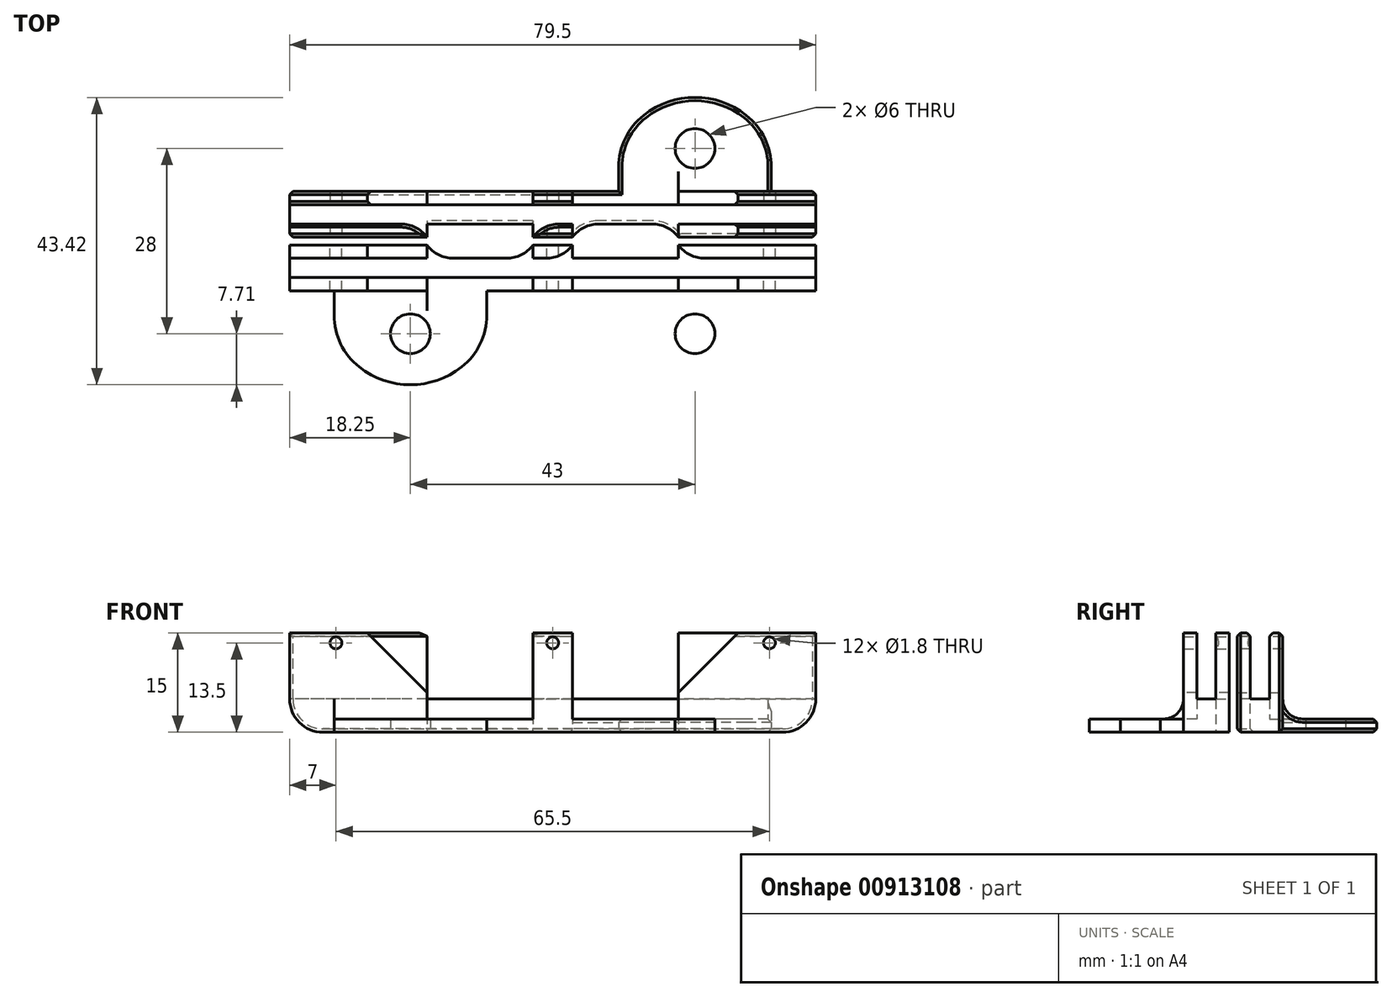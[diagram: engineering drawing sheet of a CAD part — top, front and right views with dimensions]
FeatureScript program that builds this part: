
annotation { "Feature Type Name" : "Feature", "Feature Type Description" : "" }
export const myFeature = defineFeature(function(context is Context, id is Id, definition is map)
    precondition{}
    {
        {
            var Q0;
            Q0=qCreatedBy(makeId("Top.planeOp"),FACE);
            var sketch = newSketch(context, id + "F0", { "sketchPlane" : qUnion([Q0])});
            skLineSegment(sketch, "E0", {"start": v(-39.75, 6.5) * mm, "end": v(39.75, 6.5) * mm});
            skPoint(sketch, "E1", {"position": v(-21.5, 0) * mm});
            skPoint(sketch, "E2", {"position": v(21.5, 0) * mm});
            skLineSegment(sketch, "E3", {"start": v(-21.5, 0) * mm, "end": v(21.5, 0) * mm, "construction": true});
            skLineSegment(sketch, "E4", {"start": v(0, 0) * mm, "end": v(0, 34.78) * mm, "construction": true});
            skPoint(sketch, "E5", {"position": v(0, 6.5) * mm});
            skCircle(sketch, "E6", {"center": v(-21.5, 0) * mm, "radius": 3 * mm});
            skCircle(sketch, "E7.MirrorC", {"center": v(21.5, 0) * mm, "radius": 3 * mm});
            skLineSegment(sketch, "E8", {"start": v(-21.5, 0) * mm, "end": v(-21.5, 46.29) * mm, "construction": true});
            skPoint(sketch, "E9.center.orphan", {"position": v(-21.5, -3) * mm});
            skPoint(sketch, "E10", {"position": v(-21.5, 3) * mm});
            skLineSegment(sketch, "E11", {"start": v(-39.75, 8.5) * mm, "end": v(39.75, 8.5) * mm});
            skLineSegment(sketch, "E12", {"start": v(-39.75, 6.5) * mm, "end": v(-39.75, 13.4) * mm});
            skLineSegment(sketch, "E13.MirrorCS", {"start": v(39.75, 6.5) * mm, "end": v(39.75, 13.4) * mm});
            skLineSegment(sketch, "E14", {"start": v(-39.75, 13.4) * mm, "end": v(39.75, 13.4) * mm});
            skLineSegment(sketch, "E15", {"start": v(-39.75, 11.4) * mm, "end": v(39.75, 11.4) * mm});
            skLineSegment(sketch, "E16", {"start": v(-19, 13.4) * mm, "end": v(-19, 6.5) * mm});
            skLineSegment(sketch, "E17.MirrorCS", {"start": v(19, 13.4) * mm, "end": v(19, 6.5) * mm});
            skLineSegment(sketch, "E18", {"start": v(-3, 6.5) * mm, "end": v(-3, 13.4) * mm});
            skLineSegment(sketch, "E19.MirrorCS", {"start": v(3, 6.5) * mm, "end": v(3, 13.4) * mm});
            skArc(sketch, "E20", {"start": v(-29.24, -5.03) * mm, "mid": v(-21.5, -7.71) * mm, "end": v(-13.76, -5.03) * mm});
            skLineSegment(sketch, "E21", {"start": v(-33.05, 2.82) * mm, "end": v(-33.05, 6.5) * mm});
            skLineSegment(sketch, "E22.MirrorCS", {"start": v(-9.95, 2.82) * mm, "end": v(-9.95, 6.5) * mm});
            skLineSegment(sketch, "E23.MirrorCS", {"start": v(9.95, 2.82) * mm, "end": v(9.95, 6.5) * mm});
            skLineSegment(sketch, "E24.MirrorCS", {"start": v(33.05, 2.82) * mm, "end": v(33.05, 6.5) * mm});
            skArc(sketch, "E25.MirrorCS", {"start": v(29.24, -5.03) * mm, "mid": v(21.5, -7.71) * mm, "end": v(13.76, -5.03) * mm});
            skPoint(sketch, "E26.visualSharp", {"position": v(-33.05, 0) * mm});
            skArc(sketch, "E26.filletArc", {"start": v(-33.05, 2.82) * mm, "mid": v(-32.04, -1.54) * mm, "end": v(-29.24, -5.03) * mm});
            skPoint(sketch, "E27.visualSharp", {"position": v(-9.95, 0) * mm});
            skArc(sketch, "E27.filletArc", {"start": v(-13.76, -5.03) * mm, "mid": v(-10.96, -1.54) * mm, "end": v(-9.95, 2.82) * mm});
            skPoint(sketch, "E28.visualSharp", {"position": v(9.95, 0) * mm});
            skArc(sketch, "E28.filletArc", {"start": v(9.95, 2.82) * mm, "mid": v(10.96, -1.54) * mm, "end": v(13.76, -5.03) * mm});
            skPoint(sketch, "E29.visualSharp", {"position": v(33.05, 0) * mm});
            skArc(sketch, "E29.filletArc", {"start": v(29.24, -5.03) * mm, "mid": v(32.04, -1.54) * mm, "end": v(33.05, 2.82) * mm});
            skSolve(sketch);
        }
        {
            var Q0;
            {var subQ0=sQuery(id+"F0.wireOp",EDGE,"E11");Q0=makeQuery(id+"F0.imprint","IMPRINT",FACE,{"disambiguationData":[TD([[makeQuery(id+"F0.imprint","IMPRINT",EDGE,{"derivedFrom":subQ0}),1.0]])]});}
            extrude(context, id + "F1", {"entities" : qUnion([Q0]), "depth" : 5 * mm, "offsetDistance" : 25 * mm});
        }
        {
            var Q0;
            Q0=makeQuery(id+"F0.imprint","IMPRINT",FACE,{"disambiguationData":[TD([[makeQuery(id+"F0.imprint","IMPRINT",EDGE,{"derivedFrom":sQuery(id+"F0.wireOp",EDGE,"E6")}),-1.0]])]});
            var Q1;
            Q1=makeQuery(id+"F0.imprint","IMPRINT",FACE,{"disambiguationData":[TD([[makeQuery(id+"F0.imprint","IMPRINT",EDGE,{"derivedFrom":sQuery(id+"F0.wireOp",EDGE,"E7.MirrorC")}),1.0]])]});
            var Q2;
            {var subQ1=sQuery(id+"F0.wireOp",EDGE,"E0");var subQ5=sQuery(id+"F0.wireOp",EDGE,"E19.MirrorCS");var subQ8=makeQuery(id+"F0.imprint","INTERSECT",VERTEX,{"derivedFrom":[subQ1,subQ5]});Q2=makeQuery(id+"F0.imprint","IMPRINT",FACE,{"disambiguationData":[TD([[makeQuery(id+"F0.imprint","IMPRINT",EDGE,{"disambiguationData":[TD([[subQ8,-1.0]])],"derivedFrom":subQ1}),1.0]])]});}
            var Q3;
            {var subQ1=sQuery(id+"F0.wireOp",EDGE,"E0");var subQ6=sQuery(id+"F0.wireOp",EDGE,"E17.MirrorCS");var subQ8=makeQuery(id+"F0.imprint","INTERSECT",VERTEX,{"derivedFrom":[subQ1,subQ6]});Q3=makeQuery(id+"F0.imprint","IMPRINT",FACE,{"disambiguationData":[TD([[makeQuery(id+"F0.imprint","IMPRINT",EDGE,{"disambiguationData":[TD([[subQ8,-1.0]])],"derivedFrom":subQ1}),1.0]])]});}
            var Q4;
            {var subQ0=sQuery(id+"F0.wireOp",EDGE,"E18");var subQ1=sQuery(id+"F0.wireOp",EDGE,"E0");var subQ2=makeQuery(id+"F0.imprint","INTERSECT",VERTEX,{"derivedFrom":[subQ1,subQ0]});Q4=makeQuery(id+"F0.imprint","IMPRINT",FACE,{"disambiguationData":[TD([[makeQuery(id+"F0.imprint","IMPRINT",EDGE,{"disambiguationData":[TD([[subQ2,-1.0]])],"derivedFrom":subQ1}),1.0]])]});}
            var Q5;
            {var subQ0=sQuery(id+"F0.wireOp",EDGE,"E16");var subQ1=sQuery(id+"F0.wireOp",EDGE,"E0");var subQ2=makeQuery(id+"F0.imprint","INTERSECT",VERTEX,{"derivedFrom":[subQ1,subQ0]});Q5=makeQuery(id+"F0.imprint","IMPRINT",FACE,{"disambiguationData":[TD([[makeQuery(id+"F0.imprint","IMPRINT",EDGE,{"disambiguationData":[TD([[subQ2,-1.0]])],"derivedFrom":subQ1}),1.0]])]});}
            extrude(context, id + "F2", {"entities" : qUnion([Q0, Q1, Q2, Q3, Q4, Q5]), "operationType" : NewBodyOperationType.ADD, "depth" : 2 * mm, "offsetDistance" : 25 * mm});
        }
        {
            var Q0;
            {var subQ0=sQuery(id+"F0.wireOp",EDGE,"E12");var subQ1=sQuery(id+"F0.wireOp",EDGE,"E0");var subQ2=makeQuery(id+"F0.imprint","INTERSECT",VERTEX,{"derivedFrom":[subQ1,subQ0]});Q0=makeQuery(id+"F0.imprint","IMPRINT",FACE,{"disambiguationData":[TD([[makeQuery(id+"F0.imprint","IMPRINT",EDGE,{"disambiguationData":[TD([[subQ2,-1.0]])],"derivedFrom":subQ1}),1.0]])]});}
            var Q1;
            {var subQ1=sQuery(id+"F0.wireOp",EDGE,"E0");var subQ6=sQuery(id+"F0.wireOp",EDGE,"E17.MirrorCS");var subQ8=makeQuery(id+"F0.imprint","INTERSECT",VERTEX,{"derivedFrom":[subQ1,subQ6]});Q1=makeQuery(id+"F0.imprint","IMPRINT",FACE,{"disambiguationData":[TD([[makeQuery(id+"F0.imprint","IMPRINT",EDGE,{"disambiguationData":[TD([[subQ8,-1.0]])],"derivedFrom":subQ1}),1.0]])]});}
            var Q2;
            {var subQ0=sQuery(id+"F0.wireOp",EDGE,"E14");var subQ1=sQuery(id+"F0.wireOp",EDGE,"E12");var subQ2=makeQuery(id+"F0.imprint","INTERSECT",VERTEX,{"derivedFrom":[subQ1,subQ0]});Q2=makeQuery(id+"F0.imprint","IMPRINT",FACE,{"disambiguationData":[TD([[makeQuery(id+"F0.imprint","IMPRINT",EDGE,{"disambiguationData":[TD([[subQ2,1.0]])],"derivedFrom":subQ1}),-1.0]])]});}
            var Q3;
            {var subQ0=sQuery(id+"F0.wireOp",EDGE,"E14");var subQ1=sQuery(id+"F0.wireOp",EDGE,"E13.MirrorCS");var subQ2=makeQuery(id+"F0.imprint","INTERSECT",VERTEX,{"derivedFrom":[subQ1,subQ0]});Q3=makeQuery(id+"F0.imprint","IMPRINT",FACE,{"disambiguationData":[TD([[makeQuery(id+"F0.imprint","IMPRINT",EDGE,{"disambiguationData":[TD([[subQ2,1.0]])],"derivedFrom":subQ1}),1.0]])]});}
            var Q4;
            {var subQ0=sQuery(id+"F0.wireOp",EDGE,"E18");var subQ1=sQuery(id+"F0.wireOp",EDGE,"E14");var subQ2=makeQuery(id+"F0.imprint","INTERSECT",VERTEX,{"derivedFrom":[subQ1,subQ0]});Q4=makeQuery(id+"F0.imprint","IMPRINT",FACE,{"disambiguationData":[TD([[makeQuery(id+"F0.imprint","IMPRINT",EDGE,{"disambiguationData":[TD([[subQ2,-1.0]])],"derivedFrom":subQ1}),-1.0]])]});}
            var Q5;
            {var subQ0=sQuery(id+"F0.wireOp",EDGE,"E18");var subQ1=sQuery(id+"F0.wireOp",EDGE,"E0");var subQ2=makeQuery(id+"F0.imprint","INTERSECT",VERTEX,{"derivedFrom":[subQ1,subQ0]});Q5=makeQuery(id+"F0.imprint","IMPRINT",FACE,{"disambiguationData":[TD([[makeQuery(id+"F0.imprint","IMPRINT",EDGE,{"disambiguationData":[TD([[subQ2,-1.0]])],"derivedFrom":subQ1}),1.0]])]});}
            extrude(context, id + "F3", {"entities" : qUnion([Q0, Q1, Q2, Q3, Q4, Q5]), "operationType" : NewBodyOperationType.ADD, "depth" : 15 * mm, "offsetDistance" : 25 * mm});
        }
        {
            var Q0;
            {var subQ0=sQuery(id+"F0.wireOp",EDGE,"E0");Q0=makeQuery(id+"F3.boolean.opBoolean","INTERSECT",EDGE,{"derivedFrom":[makeQuery(id+"F2.opExtrude","CAP_FACE",FACE,{"disambiguationData":[OSD([subQ0,sQuery(id+"F0.wireOp",EDGE,"E6"),sQuery(id+"F0.wireOp",EDGE,"E11"),sQuery(id+"F0.wireOp",EDGE,"E12"),sQuery(id+"F0.wireOp",EDGE,"E13.MirrorCS"),sQuery(id+"F0.wireOp",EDGE,"E20"),sQuery(id+"F0.wireOp",EDGE,"E21"),sQuery(id+"F0.wireOp",EDGE,"E22.MirrorCS"),sQuery(id+"F0.wireOp",EDGE,"E26.filletArc"),sQuery(id+"F0.wireOp",EDGE,"E27.filletArc")])],"isStart":false}),makeQuery(id+"F3.opExtrude","SWEPT_FACE",FACE,{"disambiguationData":[OSD([subQ0])]})]});}
            var Q1;
            {var subQ0=sQuery(id+"F0.wireOp",EDGE,"E0");Q1=makeQuery(id+"F2.opExtrude","CAP_EDGE",EDGE,{"disambiguationData":[OSD([subQ0]),TDD([makeQuery(id+"F0.imprint","IMPRINT",EDGE,{"disambiguationData":[TD([[makeQuery(id+"F0.imprint","INTERSECT",VERTEX,{"derivedFrom":[subQ0,sQuery(id+"F0.wireOp",EDGE,"E16")]}),1.0]])],"derivedFrom":subQ0})])],"isStart":false});}
            fillet(context, id + "F4", {"entities" : qUnion([Q0, Q1]), "radius" : 3 * mm, "tangentPropagation" : true, "allowEdgeOverflow" : false});
        }
        {
            var Q0;
            {var subQ0=sQuery(id+"F0.wireOp",EDGE,"E15");var subQ1=sQuery(id+"F0.wireOp",EDGE,"E17.MirrorCS");Q0=makeQuery(id+"F3.boolean.opBoolean","SPLIT",EDGE,{"disambiguationData":[topologyDisambiguationEdgeConnected([makeQuery(id+"F1.opExtrude","SWEPT_FACE",FACE,{"disambiguationData":[OSD([subQ0])]})])],"derivedFrom":makeQuery(id+"F3.opExtrude","SWEPT_EDGE",EDGE,{"disambiguationData":[OSD([subQ0,subQ1])]})});}
            var Q1;
            {var subQ0=sQuery(id+"F0.wireOp",EDGE,"E15");var subQ1=sQuery(id+"F0.wireOp",EDGE,"E19.MirrorCS");Q1=makeQuery(id+"F3.boolean.opBoolean","SPLIT",EDGE,{"disambiguationData":[topologyDisambiguationEdgeConnected([makeQuery(id+"F1.opExtrude","SWEPT_FACE",FACE,{"disambiguationData":[OSD([subQ0])]})])],"derivedFrom":makeQuery(id+"F3.opExtrude","SWEPT_EDGE",EDGE,{"disambiguationData":[OSD([subQ0,subQ1])]})});}
            var Q2;
            {var subQ0=sQuery(id+"F0.wireOp",EDGE,"E15");var subQ1=sQuery(id+"F0.wireOp",EDGE,"E18");Q2=makeQuery(id+"F3.boolean.opBoolean","SPLIT",EDGE,{"disambiguationData":[topologyDisambiguationEdgeConnected([makeQuery(id+"F1.opExtrude","SWEPT_FACE",FACE,{"disambiguationData":[OSD([subQ0])]})])],"derivedFrom":makeQuery(id+"F3.opExtrude","SWEPT_EDGE",EDGE,{"disambiguationData":[OSD([subQ0,subQ1])]})});}
            var Q3;
            {var subQ0=sQuery(id+"F0.wireOp",EDGE,"E15");var subQ1=sQuery(id+"F0.wireOp",EDGE,"E16");Q3=makeQuery(id+"F3.boolean.opBoolean","SPLIT",EDGE,{"disambiguationData":[topologyDisambiguationEdgeConnected([makeQuery(id+"F1.opExtrude","SWEPT_FACE",FACE,{"disambiguationData":[OSD([subQ0])]})])],"derivedFrom":makeQuery(id+"F3.opExtrude","SWEPT_EDGE",EDGE,{"disambiguationData":[OSD([subQ0,subQ1])]})});}
            fillet(context, id + "F5", {"entities" : qUnion([Q0, Q1, Q2, Q3]), "radius" : 5 * mm, "tangentPropagation" : true, "allowEdgeOverflow" : false});
        }
        {
            var Q0;
            {var subQ0=sQuery(id+"F0.wireOp",EDGE,"E14");Q0=makeQuery(id+"F3.opExtrude","SWEPT_FACE",FACE,{"disambiguationData":[OSD([subQ0]),TDD([makeQuery(id+"F0.imprint","IMPRINT",EDGE,{"disambiguationData":[TD([[makeQuery(id+"F0.imprint","INTERSECT",VERTEX,{"derivedFrom":[sQuery(id+"F0.wireOp",EDGE,"E13.MirrorCS"),subQ0]}),1.0]])],"derivedFrom":subQ0})])]});}
            var sketch = newSketch(context, id + "F6", { "sketchPlane" : qUnion([Q0])});
            skPoint(sketch, "E30", {"position": v(-32.75, 13.5) * mm});
            skPoint(sketch, "E31", {"position": v(0, 13.5) * mm});
            skPoint(sketch, "E32.MirrorP", {"position": v(32.75, 13.5) * mm});
            skSolve(sketch);
        }
        {
            var Q0;
            Q0=sQuery(id+"F6.wireOp",VERTEX,"E30");
            var Q1;
            Q1=sQuery(id+"F6.wireOp",VERTEX,"E31");
            var Q2;
            Q2=sQuery(id+"F6.wireOp",VERTEX,"E32.MirrorP");
            var Q3;
            Q3=makeQuery(id+"F1.opExtrude","SWEPT_BODY",BODY,{"disambiguationData":[OSD([sQuery(id+"F0.wireOp",EDGE,"E11"),sQuery(id+"F0.wireOp",EDGE,"E12"),sQuery(id+"F0.wireOp",EDGE,"E13.MirrorCS"),sQuery(id+"F0.wireOp",EDGE,"E15")])]});
            hole(context, id + "F7", {"style" : HoleStyle.SIMPLE, "endStyle" : HoleEndStyle.THROUGH, "holeDiameter" : 1.8 * mm, "majorDiameter" : 5 * mm, "isTappedThrough" : true, "tappedDepth" : 12 * mm, "tapClearance" : 3, "locations" : qUnion([Q0, Q1, Q2]), "scope" : qUnion([Q3])});
        }
        {
            var Q0;
            {var subQ0=sQuery(id+"F0.wireOp",EDGE,"E16");Q0=makeQuery(id+"F3.opExtrude","CAP_EDGE",EDGE,{"disambiguationData":[OSD([subQ0]),TDD([makeQuery(id+"F0.imprint","IMPRINT",EDGE,{"disambiguationData":[TD([[makeQuery(id+"F0.imprint","INTERSECT",VERTEX,{"derivedFrom":[sQuery(id+"F0.wireOp",EDGE,"E0"),subQ0]}),1.0]])],"derivedFrom":subQ0})])],"isStart":false});}
            var Q1;
            {var subQ0=sQuery(id+"F0.wireOp",EDGE,"E16");Q1=makeQuery(id+"F3.opExtrude","CAP_EDGE",EDGE,{"disambiguationData":[OSD([subQ0]),TDD([makeQuery(id+"F0.imprint","IMPRINT",EDGE,{"disambiguationData":[TD([[makeQuery(id+"F0.imprint","INTERSECT",VERTEX,{"derivedFrom":[sQuery(id+"F0.wireOp",EDGE,"E14"),subQ0]}),-1.0]])],"derivedFrom":subQ0})])],"isStart":false});}
            var Q2;
            {var subQ0=sQuery(id+"F0.wireOp",EDGE,"E17.MirrorCS");Q2=makeQuery(id+"F3.opExtrude","CAP_EDGE",EDGE,{"disambiguationData":[OSD([subQ0]),TDD([makeQuery(id+"F0.imprint","IMPRINT",EDGE,{"disambiguationData":[TD([[makeQuery(id+"F0.imprint","INTERSECT",VERTEX,{"derivedFrom":[sQuery(id+"F0.wireOp",EDGE,"E0"),subQ0]}),1.0]])],"derivedFrom":subQ0})])],"isStart":false});}
            var Q3;
            {var subQ0=sQuery(id+"F0.wireOp",EDGE,"E17.MirrorCS");Q3=makeQuery(id+"F3.opExtrude","CAP_EDGE",EDGE,{"disambiguationData":[OSD([subQ0]),TDD([makeQuery(id+"F0.imprint","IMPRINT",EDGE,{"disambiguationData":[TD([[makeQuery(id+"F0.imprint","INTERSECT",VERTEX,{"derivedFrom":[sQuery(id+"F0.wireOp",EDGE,"E14"),subQ0]}),-1.0]])],"derivedFrom":subQ0})])],"isStart":false});}
            chamfer(context, id + "F8", {"entities" : qUnion([Q0, Q1, Q2, Q3]), "width" : 9 * mm, "tangentPropagation" : true});
        }
        {
            var Q0;
            Q0=makeQuery(id+"F1.opExtrude","SWEPT_BODY",BODY,{"disambiguationData":[OSD([sQuery(id+"F0.wireOp",EDGE,"E11"),sQuery(id+"F0.wireOp",EDGE,"E12"),sQuery(id+"F0.wireOp",EDGE,"E13.MirrorCS"),sQuery(id+"F0.wireOp",EDGE,"E15")])]});
            transform(context, id + "F9", {"entities" : qUnion([Q0]), "transformType" : TransformType.TRANSLATION_3D, "dx" : 6 * mm, "dy" : 15 * mm, "dz" : 0 * mm, "makeCopy" : true});
        }
        {
            var Q0;
            Q0=makeQuery(id+"F9.opPattern","COPY",BODY,{"derivedFrom":makeQuery(id+"F1.opExtrude","SWEPT_BODY",BODY,{"disambiguationData":[OSD([sQuery(id+"F0.wireOp",EDGE,"E11"),sQuery(id+"F0.wireOp",EDGE,"E12"),sQuery(id+"F0.wireOp",EDGE,"E13.MirrorCS"),sQuery(id+"F0.wireOp",EDGE,"E15")])]}),"instanceName":"1"});
            var Q1;
            Q1=makeQuery(id+"F9.opPattern","COPY",EDGE,{"derivedFrom":makeQuery(id+"F3.opExtrude","SWEPT_EDGE",EDGE,{"disambiguationData":[OSD([sQuery(id+"F0.wireOp",EDGE,"E0"),sQuery(id+"F0.wireOp",EDGE,"E18")])]}),"instanceName":"1"});
            transform(context, id + "F10", {"entities" : qUnion([Q0]), "transformType" : TransformType.ROTATION, "transformAxis" : qUnion([Q1]), "angle" : 180 * degree, "makeCopy" : false});
        }
        {
            var Q0;
            {var subQ0=sQuery(id+"F0.wireOp",EDGE,"E12");Q0=makeQuery(id+"F3.boolean.opBoolean","MERGE",EDGE,{"derivedFrom":[makeQuery(id+"F1.opExtrude","CAP_EDGE",EDGE,{"disambiguationData":[OSD([subQ0])],"isStart":true}),makeQuery(id+"F3.opExtrude","CAP_EDGE",EDGE,{"disambiguationData":[OSD([subQ0]),TDD([makeQuery(id+"F0.imprint","IMPRINT",EDGE,{"disambiguationData":[TD([[makeQuery(id+"F0.imprint","INTERSECT",VERTEX,{"derivedFrom":[sQuery(id+"F0.wireOp",EDGE,"E0"),subQ0]}),-1.0]])],"derivedFrom":subQ0})])],"isStart":true}),makeQuery(id+"F3.opExtrude","CAP_EDGE",EDGE,{"disambiguationData":[OSD([subQ0]),TDD([makeQuery(id+"F0.imprint","IMPRINT",EDGE,{"disambiguationData":[TD([[makeQuery(id+"F0.imprint","INTERSECT",VERTEX,{"derivedFrom":[subQ0,sQuery(id+"F0.wireOp",EDGE,"E14")]}),1.0]])],"derivedFrom":subQ0})])],"isStart":true})]});}
            var Q1;
            {var subQ0=sQuery(id+"F0.wireOp",EDGE,"E13.MirrorCS");Q1=makeQuery(id+"F9.opPattern","COPY",EDGE,{"derivedFrom":makeQuery(id+"F3.boolean.opBoolean","MERGE",EDGE,{"derivedFrom":[makeQuery(id+"F2.boolean.opBoolean","MERGE",EDGE,{"derivedFrom":[makeQuery(id+"F1.opExtrude","CAP_EDGE",EDGE,{"disambiguationData":[OSD([subQ0])],"isStart":true}),makeQuery(id+"F2.opExtrude","CAP_EDGE",EDGE,{"disambiguationData":[OSD([subQ0])],"isStart":true})]}),makeQuery(id+"F3.opExtrude","CAP_EDGE",EDGE,{"disambiguationData":[OSD([subQ0]),TDD([makeQuery(id+"F0.imprint","IMPRINT",EDGE,{"disambiguationData":[TD([[makeQuery(id+"F0.imprint","INTERSECT",VERTEX,{"derivedFrom":[subQ0,sQuery(id+"F0.wireOp",EDGE,"E14")]}),1.0]])],"derivedFrom":subQ0})])],"isStart":true})]}),"instanceName":"1"});}
            var Q2;
            {var subQ0=sQuery(id+"F0.wireOp",EDGE,"E13.MirrorCS");Q2=makeQuery(id+"F3.boolean.opBoolean","MERGE",EDGE,{"derivedFrom":[makeQuery(id+"F2.boolean.opBoolean","MERGE",EDGE,{"derivedFrom":[makeQuery(id+"F1.opExtrude","CAP_EDGE",EDGE,{"disambiguationData":[OSD([subQ0])],"isStart":true}),makeQuery(id+"F2.opExtrude","CAP_EDGE",EDGE,{"disambiguationData":[OSD([subQ0])],"isStart":true})]}),makeQuery(id+"F3.opExtrude","CAP_EDGE",EDGE,{"disambiguationData":[OSD([subQ0]),TDD([makeQuery(id+"F0.imprint","IMPRINT",EDGE,{"disambiguationData":[TD([[makeQuery(id+"F0.imprint","INTERSECT",VERTEX,{"derivedFrom":[subQ0,sQuery(id+"F0.wireOp",EDGE,"E14")]}),1.0]])],"derivedFrom":subQ0})])],"isStart":true})]});}
            var Q3;
            {var subQ0=sQuery(id+"F0.wireOp",EDGE,"E12");Q3=makeQuery(id+"F9.opPattern","COPY",EDGE,{"derivedFrom":makeQuery(id+"F3.boolean.opBoolean","MERGE",EDGE,{"derivedFrom":[makeQuery(id+"F1.opExtrude","CAP_EDGE",EDGE,{"disambiguationData":[OSD([subQ0])],"isStart":true}),makeQuery(id+"F3.opExtrude","CAP_EDGE",EDGE,{"disambiguationData":[OSD([subQ0]),TDD([makeQuery(id+"F0.imprint","IMPRINT",EDGE,{"disambiguationData":[TD([[makeQuery(id+"F0.imprint","INTERSECT",VERTEX,{"derivedFrom":[sQuery(id+"F0.wireOp",EDGE,"E0"),subQ0]}),-1.0]])],"derivedFrom":subQ0})])],"isStart":true}),makeQuery(id+"F3.opExtrude","CAP_EDGE",EDGE,{"disambiguationData":[OSD([subQ0]),TDD([makeQuery(id+"F0.imprint","IMPRINT",EDGE,{"disambiguationData":[TD([[makeQuery(id+"F0.imprint","INTERSECT",VERTEX,{"derivedFrom":[subQ0,sQuery(id+"F0.wireOp",EDGE,"E14")]}),1.0]])],"derivedFrom":subQ0})])],"isStart":true})]}),"instanceName":"1"});}
            fillet(context, id + "F11", {"entities" : qUnion([Q0, Q1, Q2, Q3]), "radius" : 5 * mm, "tangentPropagation" : true, "allowEdgeOverflow" : false});
        }
        {
            var Q0;
            Q0=makeQuery(id+"F9.opPattern","COPY",EDGE,{"derivedFrom":makeQuery(id+"F2.opExtrude","CAP_EDGE",EDGE,{"disambiguationData":[OSD([sQuery(id+"F0.wireOp",EDGE,"E29.filletArc")])],"isStart":true}),"instanceName":"1"});
            var Q1;
            {var subQ0=sQuery(id+"F0.wireOp",EDGE,"E13.MirrorCS");var subQ1=sQuery(id+"F0.wireOp",EDGE,"E0");var subQ3=makeQuery(id+"F0.imprint","IMPRINT",EDGE,{"disambiguationData":[TD([[makeQuery(id+"F0.imprint","INTERSECT",VERTEX,{"derivedFrom":[subQ1,subQ0]}),1.0]])],"derivedFrom":subQ1});Q1=makeQuery(id+"F11.opFillet","BLEND_EDGE",EDGE,{"blendedFrom":[makeQuery(id+"F9.opPattern","COPY",EDGE,{"derivedFrom":makeQuery(id+"F3.boolean.opBoolean","MERGE",EDGE,{"derivedFrom":[makeQuery(id+"F2.boolean.opBoolean","MERGE",EDGE,{"derivedFrom":[makeQuery(id+"F1.opExtrude","CAP_EDGE",EDGE,{"disambiguationData":[OSD([subQ0])],"isStart":true}),makeQuery(id+"F2.opExtrude","CAP_EDGE",EDGE,{"disambiguationData":[OSD([subQ0])],"isStart":true})]}),makeQuery(id+"F3.opExtrude","CAP_EDGE",EDGE,{"disambiguationData":[OSD([subQ0]),TDD([makeQuery(id+"F0.imprint","IMPRINT",EDGE,{"disambiguationData":[TD([[makeQuery(id+"F0.imprint","INTERSECT",VERTEX,{"derivedFrom":[subQ0,sQuery(id+"F0.wireOp",EDGE,"E14")]}),1.0]])],"derivedFrom":subQ0})])],"isStart":true})]}),"instanceName":"1"}),makeQuery(id+"F9.opPattern","COPY",FACE,{"derivedFrom":makeQuery(id+"F3.boolean.opBoolean","MERGE",FACE,{"derivedFrom":[makeQuery(id+"F2.opExtrude","SWEPT_FACE",FACE,{"disambiguationData":[OSD([subQ1]),TDD([subQ3])]}),makeQuery(id+"F3.opExtrude","SWEPT_FACE",FACE,{"disambiguationData":[OSD([subQ1]),TDD([makeQuery(id+"F0.imprint","IMPRINT",EDGE,{"disambiguationData":[TD([[makeQuery(id+"F0.imprint","INTERSECT",VERTEX,{"derivedFrom":[subQ1,sQuery(id+"F0.wireOp",EDGE,"E17.MirrorCS")]}),-1.0]])],"derivedFrom":subQ1}),subQ3])]})]}),"instanceName":"1"})],"blendedInto":[makeQuery(id+"F9.opPattern","COPY",FACE,{"derivedFrom":makeQuery(id+"F3.boolean.opBoolean","MERGE",FACE,{"derivedFrom":[makeQuery(id+"F2.opExtrude","SWEPT_FACE",FACE,{"disambiguationData":[OSD([subQ1]),TDD([subQ3])]}),makeQuery(id+"F3.opExtrude","SWEPT_FACE",FACE,{"disambiguationData":[OSD([subQ1]),TDD([makeQuery(id+"F0.imprint","IMPRINT",EDGE,{"disambiguationData":[TD([[makeQuery(id+"F0.imprint","INTERSECT",VERTEX,{"derivedFrom":[subQ1,sQuery(id+"F0.wireOp",EDGE,"E17.MirrorCS")]}),-1.0]])],"derivedFrom":subQ1}),subQ3])]})]}),"instanceName":"1"})]});}
            var Q2;
            {var subQ0=sQuery(id+"F0.wireOp",EDGE,"E0");var subQ1=makeQuery(id+"F0.imprint","INTERSECT",VERTEX,{"derivedFrom":[subQ0,sQuery(id+"F0.wireOp",EDGE,"E19.MirrorCS")]});var subQ2=makeQuery(id+"F0.imprint","INTERSECT",VERTEX,{"derivedFrom":[subQ0,sQuery(id+"F0.wireOp",EDGE,"E18")]});Q2=makeQuery(id+"F9.opPattern","COPY",EDGE,{"derivedFrom":makeQuery(id+"F2.opExtrude","CAP_EDGE",EDGE,{"disambiguationData":[OSD([subQ0]),TDD([makeQuery(id+"F0.imprint","IMPRINT",EDGE,{"disambiguationData":[TD([[subQ2,1.0]])],"derivedFrom":subQ0}),makeQuery(id+"F0.imprint","IMPRINT",EDGE,{"disambiguationData":[TD([[subQ2,-1.0]])],"derivedFrom":subQ0}),makeQuery(id+"F0.imprint","IMPRINT",EDGE,{"disambiguationData":[TD([[subQ1,-1.0]])],"derivedFrom":subQ0})])],"isStart":true}),"instanceName":"1"});}
            var Q3;
            Q3=makeQuery(id+"F9.opPattern","COPY",EDGE,{"derivedFrom":makeQuery(id+"F2.opExtrude","CAP_EDGE",EDGE,{"disambiguationData":[OSD([sQuery(id+"F0.wireOp",EDGE,"E27.filletArc")])],"isStart":true}),"instanceName":"1"});
            var Q4;
            {var subQ0=sQuery(id+"F0.wireOp",EDGE,"E0");var subQ2=sQuery(id+"F0.wireOp",EDGE,"E12");var subQ3=makeQuery(id+"F0.imprint","INTERSECT",VERTEX,{"derivedFrom":[subQ0,subQ2]});Q4=makeQuery(id+"F11.opFillet","BLEND_EDGE",EDGE,{"blendedFrom":[makeQuery(id+"F9.opPattern","COPY",EDGE,{"derivedFrom":makeQuery(id+"F3.boolean.opBoolean","MERGE",EDGE,{"derivedFrom":[makeQuery(id+"F1.opExtrude","CAP_EDGE",EDGE,{"disambiguationData":[OSD([subQ2])],"isStart":true}),makeQuery(id+"F3.opExtrude","CAP_EDGE",EDGE,{"disambiguationData":[OSD([subQ2]),TDD([makeQuery(id+"F0.imprint","IMPRINT",EDGE,{"disambiguationData":[TD([[subQ3,-1.0]])],"derivedFrom":subQ2})])],"isStart":true}),makeQuery(id+"F3.opExtrude","CAP_EDGE",EDGE,{"disambiguationData":[OSD([subQ2]),TDD([makeQuery(id+"F0.imprint","IMPRINT",EDGE,{"disambiguationData":[TD([[makeQuery(id+"F0.imprint","INTERSECT",VERTEX,{"derivedFrom":[subQ2,sQuery(id+"F0.wireOp",EDGE,"E14")]}),1.0]])],"derivedFrom":subQ2})])],"isStart":true})]}),"instanceName":"1"}),makeQuery(id+"F9.opPattern","COPY",FACE,{"derivedFrom":makeQuery(id+"F3.opExtrude","SWEPT_FACE",FACE,{"disambiguationData":[OSD([subQ0]),TDD([makeQuery(id+"F0.imprint","IMPRINT",EDGE,{"disambiguationData":[TD([[subQ3,-1.0]])],"derivedFrom":subQ0}),makeQuery(id+"F0.imprint","IMPRINT",EDGE,{"disambiguationData":[TD([[makeQuery(id+"F0.imprint","INTERSECT",VERTEX,{"derivedFrom":[subQ0,sQuery(id+"F0.wireOp",EDGE,"E16")]}),1.0]])],"derivedFrom":subQ0})])]}),"instanceName":"1"})],"blendedInto":[makeQuery(id+"F9.opPattern","COPY",FACE,{"derivedFrom":makeQuery(id+"F3.opExtrude","SWEPT_FACE",FACE,{"disambiguationData":[OSD([subQ0]),TDD([makeQuery(id+"F0.imprint","IMPRINT",EDGE,{"disambiguationData":[TD([[subQ3,-1.0]])],"derivedFrom":subQ0}),makeQuery(id+"F0.imprint","IMPRINT",EDGE,{"disambiguationData":[TD([[makeQuery(id+"F0.imprint","INTERSECT",VERTEX,{"derivedFrom":[subQ0,sQuery(id+"F0.wireOp",EDGE,"E16")]}),1.0]])],"derivedFrom":subQ0})])]}),"instanceName":"1"})]});}
            var Q5;
            {var subQ0=sQuery(id+"F0.wireOp",EDGE,"E14");Q5=makeQuery(id+"F9.opPattern","COPY",EDGE,{"derivedFrom":makeQuery(id+"F3.opExtrude","CAP_EDGE",EDGE,{"disambiguationData":[OSD([subQ0]),TDD([makeQuery(id+"F0.imprint","IMPRINT",EDGE,{"disambiguationData":[TD([[makeQuery(id+"F0.imprint","INTERSECT",VERTEX,{"derivedFrom":[sQuery(id+"F0.wireOp",EDGE,"E12"),subQ0]}),-1.0]])],"derivedFrom":subQ0})])],"isStart":true}),"instanceName":"1"});}
            var Q6;
            {var subQ0=sQuery(id+"F0.wireOp",EDGE,"E15");var subQ1=sQuery(id+"F0.wireOp",EDGE,"E14");var subQ2=sQuery(id+"F0.wireOp",EDGE,"E13.MirrorCS");var subQ3=sQuery(id+"F0.wireOp",EDGE,"E16");var subQ4=sQuery(id+"F0.wireOp",EDGE,"E12");var subQ5=sQuery(id+"F0.wireOp",EDGE,"E11");var subQ6=sQuery(id+"F0.wireOp",EDGE,"E0");Q6=makeQuery(id+"F9.opPattern","COPY",EDGE,{"derivedFrom":makeQuery(id+"F5.opFillet","BLEND_EDGE",EDGE,{"blendedFrom":[makeQuery(id+"F3.boolean.opBoolean","SPLIT",EDGE,{"disambiguationData":[topologyDisambiguationEdgeConnected([makeQuery(id+"F1.opExtrude","SWEPT_FACE",FACE,{"disambiguationData":[OSD([subQ0])]})])],"derivedFrom":makeQuery(id+"F3.opExtrude","SWEPT_EDGE",EDGE,{"disambiguationData":[OSD([subQ0,subQ3])]})}),makeQuery(id+"F3.boolean.opBoolean","MERGE",FACE,{"derivedFrom":[makeQuery(id+"F2.boolean.opBoolean","MERGE",FACE,{"derivedFrom":[makeQuery(id+"F1.opExtrude","CAP_FACE",FACE,{"disambiguationData":[OSD([subQ5,subQ4,subQ2,subQ0])],"isStart":true}),makeQuery(id+"F2.opExtrude","CAP_FACE",FACE,{"disambiguationData":[OSD([subQ6,sQuery(id+"F0.wireOp",EDGE,"E6"),sQuery(id+"F0.wireOp",EDGE,"E7.MirrorC"),subQ5,subQ2,subQ3,sQuery(id+"F0.wireOp",EDGE,"E20"),sQuery(id+"F0.wireOp",EDGE,"E21"),sQuery(id+"F0.wireOp",EDGE,"E22.MirrorCS"),sQuery(id+"F0.wireOp",EDGE,"E23.MirrorCS"),sQuery(id+"F0.wireOp",EDGE,"E24.MirrorCS"),sQuery(id+"F0.wireOp",EDGE,"E25.MirrorCS"),sQuery(id+"F0.wireOp",EDGE,"E26.filletArc"),sQuery(id+"F0.wireOp",EDGE,"E27.filletArc"),sQuery(id+"F0.wireOp",EDGE,"E28.filletArc"),sQuery(id+"F0.wireOp",EDGE,"E29.filletArc")])],"isStart":true})]}),makeQuery(id+"F3.opExtrude","CAP_FACE",FACE,{"disambiguationData":[OSD([subQ6,subQ5,subQ4,subQ3])],"isStart":true}),makeQuery(id+"F3.opExtrude","CAP_FACE",FACE,{"disambiguationData":[OSD([subQ4,subQ1,subQ0,subQ3])],"isStart":true}),makeQuery(id+"F3.opExtrude","CAP_FACE",FACE,{"disambiguationData":[OSD([subQ2,subQ1,subQ0,sQuery(id+"F0.wireOp",EDGE,"E17.MirrorCS")])],"isStart":true}),makeQuery(id+"F3.opExtrude","CAP_FACE",FACE,{"disambiguationData":[OSD([subQ1,subQ0,sQuery(id+"F0.wireOp",EDGE,"E18"),sQuery(id+"F0.wireOp",EDGE,"E19.MirrorCS")])],"isStart":true})]})],"blendedInto":[makeQuery(id+"F3.boolean.opBoolean","MERGE",FACE,{"derivedFrom":[makeQuery(id+"F2.boolean.opBoolean","MERGE",FACE,{"derivedFrom":[makeQuery(id+"F1.opExtrude","CAP_FACE",FACE,{"disambiguationData":[OSD([subQ5,subQ4,subQ2,subQ0])],"isStart":true}),makeQuery(id+"F2.opExtrude","CAP_FACE",FACE,{"disambiguationData":[OSD([subQ6,sQuery(id+"F0.wireOp",EDGE,"E6"),sQuery(id+"F0.wireOp",EDGE,"E7.MirrorC"),subQ5,subQ2,subQ3,sQuery(id+"F0.wireOp",EDGE,"E20"),sQuery(id+"F0.wireOp",EDGE,"E21"),sQuery(id+"F0.wireOp",EDGE,"E22.MirrorCS"),sQuery(id+"F0.wireOp",EDGE,"E23.MirrorCS"),sQuery(id+"F0.wireOp",EDGE,"E24.MirrorCS"),sQuery(id+"F0.wireOp",EDGE,"E25.MirrorCS"),sQuery(id+"F0.wireOp",EDGE,"E26.filletArc"),sQuery(id+"F0.wireOp",EDGE,"E27.filletArc"),sQuery(id+"F0.wireOp",EDGE,"E28.filletArc"),sQuery(id+"F0.wireOp",EDGE,"E29.filletArc")])],"isStart":true})]}),makeQuery(id+"F3.opExtrude","CAP_FACE",FACE,{"disambiguationData":[OSD([subQ6,subQ5,subQ4,subQ3])],"isStart":true}),makeQuery(id+"F3.opExtrude","CAP_FACE",FACE,{"disambiguationData":[OSD([subQ4,subQ1,subQ0,subQ3])],"isStart":true}),makeQuery(id+"F3.opExtrude","CAP_FACE",FACE,{"disambiguationData":[OSD([subQ2,subQ1,subQ0,sQuery(id+"F0.wireOp",EDGE,"E17.MirrorCS")])],"isStart":true}),makeQuery(id+"F3.opExtrude","CAP_FACE",FACE,{"disambiguationData":[OSD([subQ1,subQ0,sQuery(id+"F0.wireOp",EDGE,"E18"),sQuery(id+"F0.wireOp",EDGE,"E19.MirrorCS")])],"isStart":true})]})]}),"instanceName":"1"});}
            var Q7;
            {var subQ0=sQuery(id+"F0.wireOp",EDGE,"E14");Q7=makeQuery(id+"F9.opPattern","COPY",EDGE,{"derivedFrom":makeQuery(id+"F3.opExtrude","CAP_EDGE",EDGE,{"disambiguationData":[OSD([subQ0]),TDD([makeQuery(id+"F0.imprint","IMPRINT",EDGE,{"disambiguationData":[TD([[makeQuery(id+"F0.imprint","INTERSECT",VERTEX,{"derivedFrom":[subQ0,sQuery(id+"F0.wireOp",EDGE,"E18")]}),-1.0]])],"derivedFrom":subQ0})])],"isStart":true}),"instanceName":"1"});}
            var Q8;
            {var subQ5=sQuery(id+"F0.wireOp",EDGE,"E15");var subQ7=sQuery(id+"F0.wireOp",EDGE,"E14");var subQ8=sQuery(id+"F0.wireOp",EDGE,"E17.MirrorCS");Q8=makeQuery(id+"F9.opPattern","COPY",EDGE,{"derivedFrom":makeQuery(id+"F3.boolean.opBoolean","SPLIT",EDGE,{"disambiguationData":[TD([makeQuery(id+"F3.opExtrude","SWEPT_FACE",FACE,{"disambiguationData":[OSD([subQ8]),TDD([makeQuery(id+"F0.imprint","IMPRINT",EDGE,{"disambiguationData":[TD([[makeQuery(id+"F0.imprint","INTERSECT",VERTEX,{"derivedFrom":[subQ7,subQ8]}),-1.0]])],"derivedFrom":subQ8})])]})])],"derivedFrom":makeQuery(id+"F1.opExtrude","CAP_EDGE",EDGE,{"disambiguationData":[OSD([subQ5])],"isStart":true})}),"instanceName":"1"});}
            var Q9;
            {var subQ0=sQuery(id+"F0.wireOp",EDGE,"E14");Q9=makeQuery(id+"F9.opPattern","COPY",EDGE,{"derivedFrom":makeQuery(id+"F3.opExtrude","CAP_EDGE",EDGE,{"disambiguationData":[OSD([subQ0]),TDD([makeQuery(id+"F0.imprint","IMPRINT",EDGE,{"disambiguationData":[TD([[makeQuery(id+"F0.imprint","INTERSECT",VERTEX,{"derivedFrom":[sQuery(id+"F0.wireOp",EDGE,"E13.MirrorCS"),subQ0]}),1.0]])],"derivedFrom":subQ0})])],"isStart":true}),"instanceName":"1"});}
            var Q10;
            {var subQ0=sQuery(id+"F0.wireOp",EDGE,"E0");Q10=makeQuery(id+"F9.opPattern","COPY",EDGE,{"derivedFrom":makeQuery(id+"F3.opExtrude","CAP_EDGE",EDGE,{"disambiguationData":[OSD([subQ0]),TDD([makeQuery(id+"F0.imprint","IMPRINT",EDGE,{"disambiguationData":[TD([[makeQuery(id+"F0.imprint","INTERSECT",VERTEX,{"derivedFrom":[subQ0,sQuery(id+"F0.wireOp",EDGE,"E12")]}),-1.0]])],"derivedFrom":subQ0}),makeQuery(id+"F0.imprint","IMPRINT",EDGE,{"disambiguationData":[TD([[makeQuery(id+"F0.imprint","INTERSECT",VERTEX,{"derivedFrom":[subQ0,sQuery(id+"F0.wireOp",EDGE,"E16")]}),1.0]])],"derivedFrom":subQ0})])],"isStart":false}),"instanceName":"1"});}
            var Q11;
            {var subQ0=sQuery(id+"F0.wireOp",EDGE,"E11");Q11=makeQuery(id+"F9.opPattern","COPY",EDGE,{"derivedFrom":makeQuery(id+"F3.opExtrude","CAP_EDGE",EDGE,{"disambiguationData":[OSD([subQ0]),TDD([makeQuery(id+"F0.imprint","IMPRINT",EDGE,{"disambiguationData":[TD([[makeQuery(id+"F0.imprint","INTERSECT",VERTEX,{"derivedFrom":[subQ0,sQuery(id+"F0.wireOp",EDGE,"E12")]}),-1.0]])],"derivedFrom":subQ0})])],"isStart":false}),"instanceName":"1"});}
            var Q12;
            {var subQ0=sQuery(id+"F0.wireOp",EDGE,"E15");Q12=makeQuery(id+"F9.opPattern","COPY",EDGE,{"derivedFrom":makeQuery(id+"F3.opExtrude","CAP_EDGE",EDGE,{"disambiguationData":[OSD([subQ0]),TDD([makeQuery(id+"F0.imprint","IMPRINT",EDGE,{"disambiguationData":[TD([[makeQuery(id+"F0.imprint","INTERSECT",VERTEX,{"derivedFrom":[sQuery(id+"F0.wireOp",EDGE,"E12"),subQ0]}),-1.0]])],"derivedFrom":subQ0})])],"isStart":false}),"instanceName":"1"});}
            var Q13;
            {var subQ0=sQuery(id+"F0.wireOp",EDGE,"E14");Q13=makeQuery(id+"F9.opPattern","COPY",EDGE,{"derivedFrom":makeQuery(id+"F3.opExtrude","CAP_EDGE",EDGE,{"disambiguationData":[OSD([subQ0]),TDD([makeQuery(id+"F0.imprint","IMPRINT",EDGE,{"disambiguationData":[TD([[makeQuery(id+"F0.imprint","INTERSECT",VERTEX,{"derivedFrom":[sQuery(id+"F0.wireOp",EDGE,"E12"),subQ0]}),-1.0]])],"derivedFrom":subQ0})])],"isStart":false}),"instanceName":"1"});}
            var Q14;
            {var subQ0=sQuery(id+"F0.wireOp",EDGE,"E0");Q14=makeQuery(id+"F9.opPattern","COPY",EDGE,{"derivedFrom":makeQuery(id+"F3.opExtrude","CAP_EDGE",EDGE,{"disambiguationData":[OSD([subQ0]),TDD([makeQuery(id+"F0.imprint","IMPRINT",EDGE,{"disambiguationData":[TD([[makeQuery(id+"F0.imprint","INTERSECT",VERTEX,{"derivedFrom":[subQ0,sQuery(id+"F0.wireOp",EDGE,"E18")]}),-1.0]])],"derivedFrom":subQ0})])],"isStart":false}),"instanceName":"1"});}
            var Q15;
            {var subQ0=sQuery(id+"F0.wireOp",EDGE,"E11");Q15=makeQuery(id+"F9.opPattern","COPY",EDGE,{"derivedFrom":makeQuery(id+"F3.opExtrude","CAP_EDGE",EDGE,{"disambiguationData":[OSD([subQ0]),TDD([makeQuery(id+"F0.imprint","IMPRINT",EDGE,{"disambiguationData":[TD([[makeQuery(id+"F0.imprint","INTERSECT",VERTEX,{"derivedFrom":[subQ0,sQuery(id+"F0.wireOp",EDGE,"E18")]}),-1.0]])],"derivedFrom":subQ0})])],"isStart":false}),"instanceName":"1"});}
            var Q16;
            {var subQ0=sQuery(id+"F0.wireOp",EDGE,"E0");Q16=makeQuery(id+"F9.opPattern","COPY",EDGE,{"derivedFrom":makeQuery(id+"F3.opExtrude","CAP_EDGE",EDGE,{"disambiguationData":[OSD([subQ0]),TDD([makeQuery(id+"F0.imprint","IMPRINT",EDGE,{"disambiguationData":[TD([[makeQuery(id+"F0.imprint","INTERSECT",VERTEX,{"derivedFrom":[subQ0,sQuery(id+"F0.wireOp",EDGE,"E17.MirrorCS")]}),-1.0]])],"derivedFrom":subQ0}),makeQuery(id+"F0.imprint","IMPRINT",EDGE,{"disambiguationData":[TD([[makeQuery(id+"F0.imprint","INTERSECT",VERTEX,{"derivedFrom":[subQ0,sQuery(id+"F0.wireOp",EDGE,"E13.MirrorCS")]}),1.0]])],"derivedFrom":subQ0})])],"isStart":false}),"instanceName":"1"});}
            var Q17;
            {var subQ0=sQuery(id+"F0.wireOp",EDGE,"E11");Q17=makeQuery(id+"F9.opPattern","COPY",EDGE,{"derivedFrom":makeQuery(id+"F3.opExtrude","CAP_EDGE",EDGE,{"disambiguationData":[OSD([subQ0]),TDD([makeQuery(id+"F0.imprint","IMPRINT",EDGE,{"disambiguationData":[TD([[makeQuery(id+"F0.imprint","INTERSECT",VERTEX,{"derivedFrom":[subQ0,sQuery(id+"F0.wireOp",EDGE,"E13.MirrorCS")]}),1.0]])],"derivedFrom":subQ0})])],"isStart":false}),"instanceName":"1"});}
            var Q18;
            {var subQ0=sQuery(id+"F0.wireOp",EDGE,"E15");Q18=makeQuery(id+"F9.opPattern","COPY",EDGE,{"derivedFrom":makeQuery(id+"F3.opExtrude","CAP_EDGE",EDGE,{"disambiguationData":[OSD([subQ0]),TDD([makeQuery(id+"F0.imprint","IMPRINT",EDGE,{"disambiguationData":[TD([[makeQuery(id+"F0.imprint","INTERSECT",VERTEX,{"derivedFrom":[sQuery(id+"F0.wireOp",EDGE,"E13.MirrorCS"),subQ0]}),1.0]])],"derivedFrom":subQ0})])],"isStart":false}),"instanceName":"1"});}
            var Q19;
            {var subQ0=sQuery(id+"F0.wireOp",EDGE,"E14");Q19=makeQuery(id+"F9.opPattern","COPY",EDGE,{"derivedFrom":makeQuery(id+"F3.opExtrude","CAP_EDGE",EDGE,{"disambiguationData":[OSD([subQ0]),TDD([makeQuery(id+"F0.imprint","IMPRINT",EDGE,{"disambiguationData":[TD([[makeQuery(id+"F0.imprint","INTERSECT",VERTEX,{"derivedFrom":[sQuery(id+"F0.wireOp",EDGE,"E13.MirrorCS"),subQ0]}),1.0]])],"derivedFrom":subQ0})])],"isStart":false}),"instanceName":"1"});}
            var Q20;
            {var subQ0=sQuery(id+"F0.wireOp",EDGE,"E14");Q20=makeQuery(id+"F9.opPattern","COPY",EDGE,{"derivedFrom":makeQuery(id+"F3.opExtrude","CAP_EDGE",EDGE,{"disambiguationData":[OSD([subQ0]),TDD([makeQuery(id+"F0.imprint","IMPRINT",EDGE,{"disambiguationData":[TD([[makeQuery(id+"F0.imprint","INTERSECT",VERTEX,{"derivedFrom":[subQ0,sQuery(id+"F0.wireOp",EDGE,"E18")]}),-1.0]])],"derivedFrom":subQ0})])],"isStart":false}),"instanceName":"1"});}
            var Q21;
            {var subQ0=sQuery(id+"F0.wireOp",EDGE,"E15");Q21=makeQuery(id+"F9.opPattern","COPY",EDGE,{"derivedFrom":makeQuery(id+"F3.opExtrude","CAP_EDGE",EDGE,{"disambiguationData":[OSD([subQ0]),TDD([makeQuery(id+"F0.imprint","IMPRINT",EDGE,{"disambiguationData":[TD([[makeQuery(id+"F0.imprint","INTERSECT",VERTEX,{"derivedFrom":[subQ0,sQuery(id+"F0.wireOp",EDGE,"E18")]}),-1.0]])],"derivedFrom":subQ0})])],"isStart":false}),"instanceName":"1"});}
            var Q22;
            Q22=makeQuery(id+"F9.opPattern","COPY",EDGE,{"derivedFrom":makeQuery(id+"F2.opExtrude","CAP_EDGE",EDGE,{"disambiguationData":[OSD([sQuery(id+"F0.wireOp",EDGE,"E26.filletArc")])],"isStart":false}),"instanceName":"1"});
            var Q23;
            Q23=makeQuery(id+"F9.opPattern","COPY",EDGE,{"derivedFrom":makeQuery(id+"F2.opExtrude","CAP_EDGE",EDGE,{"disambiguationData":[OSD([sQuery(id+"F0.wireOp",EDGE,"E28.filletArc")])],"isStart":false}),"instanceName":"1"});
            var Q24;
            {var subQ0=sQuery(id+"F0.wireOp",EDGE,"E18");var subQ1=sQuery(id+"F0.wireOp",EDGE,"E0");var subQ2=makeQuery(id+"F0.imprint","INTERSECT",VERTEX,{"derivedFrom":[subQ1,subQ0]});var subQ3=makeQuery(id+"F0.imprint","INTERSECT",VERTEX,{"derivedFrom":[subQ1,sQuery(id+"F0.wireOp",EDGE,"E19.MirrorCS")]});var subQ4=makeQuery(id+"F0.imprint","IMPRINT",EDGE,{"disambiguationData":[TD([[subQ2,-1.0]])],"derivedFrom":subQ1});var subQ6=makeQuery(id+"F0.imprint","IMPRINT",EDGE,{"disambiguationData":[TD([[subQ3,-1.0]])],"derivedFrom":subQ1});var subQ7=sQuery(id+"F0.wireOp",EDGE,"E22.MirrorCS");var subQ8=makeQuery(id+"F0.imprint","IMPRINT",EDGE,{"disambiguationData":[TD([[subQ2,1.0]])],"derivedFrom":subQ1});Q24=makeQuery(id+"F9.opPattern","COPY",EDGE,{"derivedFrom":makeQuery(id+"F3.boolean.opBoolean","SPLIT",EDGE,{"disambiguationData":[TD([makeQuery(id+"F2.opExtrude","SWEPT_FACE",FACE,{"disambiguationData":[OSD([subQ7])]})])],"derivedFrom":makeQuery(id+"F2.opExtrude","CAP_EDGE",EDGE,{"disambiguationData":[OSD([subQ1]),TDD([subQ8,subQ4,subQ6])],"isStart":false})}),"instanceName":"1"});}
            var Q25;
            {var subQ0=sQuery(id+"F0.wireOp",EDGE,"E0");var subQ1=makeQuery(id+"F0.imprint","INTERSECT",VERTEX,{"derivedFrom":[subQ0,sQuery(id+"F0.wireOp",EDGE,"E18")]});var subQ2=sQuery(id+"F0.wireOp",EDGE,"E19.MirrorCS");var subQ3=makeQuery(id+"F0.imprint","INTERSECT",VERTEX,{"derivedFrom":[subQ0,subQ2]});var subQ4=makeQuery(id+"F0.imprint","IMPRINT",EDGE,{"disambiguationData":[TD([[subQ1,-1.0]])],"derivedFrom":subQ0});var subQ5=sQuery(id+"F0.wireOp",EDGE,"E23.MirrorCS");var subQ8=makeQuery(id+"F0.imprint","IMPRINT",EDGE,{"disambiguationData":[TD([[subQ3,-1.0]])],"derivedFrom":subQ0});var subQ9=makeQuery(id+"F0.imprint","IMPRINT",EDGE,{"disambiguationData":[TD([[subQ1,1.0]])],"derivedFrom":subQ0});Q25=makeQuery(id+"F9.opPattern","COPY",EDGE,{"derivedFrom":makeQuery(id+"F3.boolean.opBoolean","SPLIT",EDGE,{"disambiguationData":[TD([makeQuery(id+"F2.opExtrude","SWEPT_FACE",FACE,{"disambiguationData":[OSD([subQ5])]})])],"derivedFrom":makeQuery(id+"F2.opExtrude","CAP_EDGE",EDGE,{"disambiguationData":[OSD([subQ0]),TDD([subQ9,subQ4,subQ8])],"isStart":false})}),"instanceName":"1"});}
            chamfer(context, id + "F12", {"entities" : qUnion([Q0, Q1, Q2, Q3, Q4, Q5, Q6, Q7, Q8, Q9, Q10, Q11, Q12, Q13, Q14, Q15, Q16, Q17, Q18, Q19, Q20, Q21, Q22, Q23, Q24, Q25]), "width" : 0.5 * mm, "tangentPropagation" : true});
        }
    });
